MODEL slx_0e36ac3a5637
KIND model
CONFIG AbsTol = auto
CONFIG EnableMultiTasking = off
CONFIG FixedStep = auto
CONFIG MaxStep = auto
CONFIG MinStep = auto
CONFIG RelTol = 1e-3
CONFIG SampleTimeConstraint = Unconstrained
CONFIG SolverName = VariableStepAuto
CONFIG StartTime = 0.0
CONFIG StopTime = 10
BLOCK [Reference] Brine  REF=customization_lib/solution/elements/Reservoir (SS)
  SourceBlock = customization_lib/solution/elements/Reservoir (SS)
  SourceProductName = Customization
  SourceType = Reservoir (SS)
BLOCK [BusCreator] Bus Creator
  DisplayOption = bar
  InheritFromInputs = on
  Inputs = 2
BLOCK [Reference] Feed  REF=customization_lib/solution/elements/Reservoir (SS)
  SourceBlock = customization_lib/solution/elements/Reservoir (SS)
  SourceProductName = Customization
  SourceType = Reservoir (SS)
BLOCK [Reference] Feed Pump  REF=customization_lib/solution/sources/Flow Rate Source
(SS)
  SourceBlock = customization_lib/solution/sources/Flow Rate Source\n(SS)
  SourceProductName = Customization
  SourceType = Flow Rate Source\n(SS)
BLOCK [Reference] PS Sine Wave  REF=fl_lib/Physical Signals/Sources/PS Sine Wave
  SourceBlock = fl_lib/Physical Signals/Sources/PS Sine Wave
  SourceType = PS Sine Wave
BLOCK [Reference] Pressure Relief Valve (SS)  REF=customization_lib/solution/elements/Pressure Relief
Valve (SS)
  NameLocation = right
  SourceBlock = customization_lib/solution/elements/Pressure Relief\nValve (SS)
  SourceProductName = Customization
  SourceType = Pressure Relief\nValve (SS)
BLOCK [SimscapeProbe] Probe
  BoundBlock = 34
  Variables = {"P.x":{"Probing":"ON"}}
BLOCK [SimscapeProbe] Probe1
  BoundBlock = 29
  Variables = {"mdot_A":{"Probing":"ON"}}
BLOCK [Reference] Resistance  REF=customization_lib/solution/elements/Linear Resistance
(SS)
  SourceBlock = customization_lib/solution/elements/Linear Resistance\n(SS)
  SourceProductName = Customization
  SourceType = Linear Resistance\n(SS)
BLOCK [Reference] Solver Configuration  REF=nesl_utility/Solver
Configuration
  SourceBlock = nesl_utility/Solver\nConfiguration
  SourceType = Solver\nConfiguration
BLOCK [ToWorkspace] To Workspace
  FixptAsFi = on
  MaxDataPoints = inf
  SampleTime = -1
  SaveFormat = Timeseries
  VariableName = simout
BLOCK [Reference] Waste  REF=customization_lib/solution/elements/Reservoir (SS)
  SourceBlock = customization_lib/solution/elements/Reservoir (SS)
  SourceProductName = Customization
  SourceType = Reservoir (SS)
BLOCK [Reference] Water  REF=customization_lib/solution/elements/Reservoir (SS)
  SourceBlock = customization_lib/solution/elements/Reservoir (SS)
  SourceProductName = Customization
  SourceType = Reservoir (SS)
BLOCK [Reference] membrane  REF=customization_lib/membranes/Membrane (SS)
  SourceBlock = customization_lib/membranes/Membrane (SS)
  SourceProductName = Customization
  SourceType = Membrane (SS)
ANNOTATION (root): <copyright redacted>
LINE Bus Creator:1 -> To Workspace:1
LINE Probe1:1 -> Bus Creator:1
LINE Probe:1 -> Bus Creator:2
PLINE Brine:LConn1 -- Resistance:RConn1
PLINE Feed Pump:LConn1 -- Feed:LConn1
PLINE Feed Pump:LConn2 -- PS Sine Wave:RConn1
PNET net1: Feed Pump:RConn1 -- Pressure Relief Valve (SS):LConn1 -- Solver Configuration:RConn1 -- membrane:LConn1
PLINE Pressure Relief Valve (SS):RConn1 -- Waste:LConn1
PLINE Resistance:LConn1 -- membrane:RConn1
PLINE Water:LConn1 -- membrane:RConn2
note: PNET lines group multi-terminal physical nets as a canonical sorted terminal list (undirected conserving connections); 2-terminal nets keep the pairwise PLINE form
